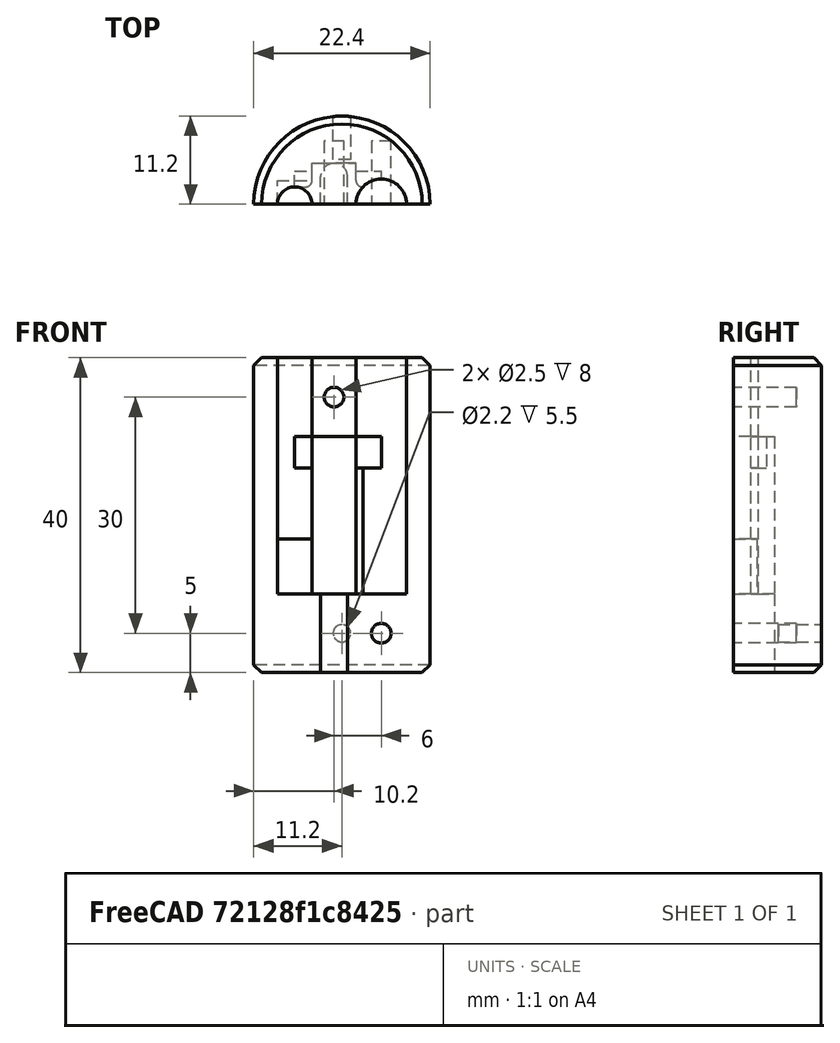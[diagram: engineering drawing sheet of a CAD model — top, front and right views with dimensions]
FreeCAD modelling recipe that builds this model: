
FCSTD DOCUMENT  (FreeCAD 0.21R33771 (Git))
Label: J-Pole_433_Bot2
Comment: J-Pole antenna bottom shell 2 (cable leading part)
License: CC BY-SA 4.0 (SPDX-ID: CC-BY-SA-4.0)
LicenseURL: https://creativecommons.org/licenses/by-sa/4.0/legalcode.txt
objects: Sketcher::SketchObject×9, PartDesign::Pocket×8, PartDesign::Fillet×2, PartDesign::Pad×1, PartDesign::Chamfer×1, PartDesign::Body×1, Mesh::Feature×1
note: 34 computed .brp shape members not serialized (recipe doc carries the construction recipe); baked Part::Feature solids carry a one-line shape summary decoded from their .brp

FEATURE [Sketcher::SketchObject] Sketch
  FullyConstrained = true
  MapMode = 5
  Support = -> [XY_Plane]
  sketch-geometry (2):
    g0: LineSegment StartX=-11.2 StartY=-2.98e-14 StartZ=0 EndX=11.2 EndY=-2.98e-14 EndZ=0
    g1: ArcOfCircle CenterX=0 CenterY=0 CenterZ=0 NormalX=0 NormalY=0 NormalZ=1 AngleXU=0 Radius=11.2 StartAngle=-2.7e-15 EndAngle=3.14159
  constraints (6):
    c: PointOnObject(g0,g-1)
    c: Horizontal(g0)
    c: Coincident(g1,g-1)
    c: Coincident(g1,g0)
    c: Coincident(g1,g0)
    c: Radius(g1) = 11.2
FEATURE [PartDesign::Pad] Pad
  Direction = (0,0,1)
  Length = 40
  Length2 = 10
  Profile = -> Sketch
  ReferenceAxis = -> Sketch [N_Axis]
  Type = 0
FEATURE [Sketcher::SketchObject] Sketch001
  ExternalGeometry = -> [Pad]
  FullyConstrained = true
  MapMode = 5
  Placement = pos=(0,0,40) rot=(0,0,1;0rad)
  Support = -> [Pad]
  sketch-geometry (2):
    g0: Circle CenterX=-6 CenterY=-2.98e-14 CenterZ=0 NormalX=0 NormalY=0 NormalZ=1 AngleXU=0 Radius=2.2
    g1: Circle CenterX=5 CenterY=-2.98e-14 CenterZ=0 NormalX=0 NormalY=0 NormalZ=1 AngleXU=0 Radius=3.2
  constraints (6):
    c: PointOnObject(g0,g-3)
    c: PointOnObject(g1,g-3)
    c: Radius(g1) = 3.2
    c: Radius(g0) = 2.2
    c: Distance(g-1,g0) = 6
    c: Distance(g-1,g1) = 5
FEATURE [PartDesign::Pocket] Pocket
  BaseFeature = -> Pad
  Direction = (0,0,-1)
  Length = 30
  Length2 = 5
  Profile = -> Sketch001
  ReferenceAxis = -> Sketch001 [N_Axis]
  Type = 0
FEATURE [Sketcher::SketchObject] Sketch002
  ExternalGeometry = -> [Pocket]
  FullyConstrained = true
  MapMode = 5
  Placement = pos=(0,-2.98e-14,0) rot=(1,0,0;1.5708rad)
  Support = -> [Pocket]
  sketch-geometry (4):
    g0: LineSegment StartX=-6 StartY=30 StartZ=0 EndX=5 EndY=30 EndZ=0
    g1: LineSegment StartX=5 StartY=30 StartZ=0 EndX=5 EndY=10 EndZ=0
    g2: LineSegment StartX=5 StartY=10 StartZ=0 EndX=-6 EndY=10 EndZ=0
    g3: LineSegment StartX=-6 StartY=10 StartZ=0 EndX=-6 EndY=30 EndZ=0
  constraints (12):
    c: Coincident(g0,g1)
    c: Coincident(g1,g2)
    c: Coincident(g2,g3)
    c: Coincident(g3,g0)
    c: Horizontal(g0)
    c: Horizontal(g2)
    c: Vertical(g1)
    c: Vertical(g3)
    c: PointOnObject(g-3,g2)
    c: DistanceX(g-2,g2) = -6
    c: DistanceX(g-2,g1) = 5
    c: DistanceY(g1,g1) = 20
FEATURE [PartDesign::Pocket] Pocket001
  BaseFeature = -> Pocket
  Direction = (0,1,-2e-16)
  Length = 2.2
  Length2 = 5
  Profile = -> Sketch002
  ReferenceAxis = -> Sketch002 [N_Axis]
  Type = 0
FEATURE [Sketcher::SketchObject] Sketch003
  ExternalGeometry = -> [Pocket001]
  FullyConstrained = true
  MapMode = 5
  Placement = pos=(0,-2.98e-14,0) rot=(1,0,0;1.5708rad)
  Support = -> [Pocket001]
  sketch-geometry (4):
    g0: LineSegment StartX=-2.7 StartY=10 StartZ=0 EndX=0.7 EndY=10 EndZ=0
    g1: LineSegment StartX=0.7 StartY=10 StartZ=0 EndX=0.7 EndY=0 EndZ=0
    g2: LineSegment StartX=0.7 StartY=0 StartZ=0 EndX=-2.7 EndY=0 EndZ=0
    g3: LineSegment StartX=-2.7 StartY=0 StartZ=0 EndX=-2.7 EndY=10 EndZ=0
  constraints (12):
    c: Coincident(g0,g1)
    c: Coincident(g1,g2)
    c: Coincident(g2,g3)
    c: Coincident(g3,g0)
    c: Horizontal(g0)
    c: Horizontal(g2)
    c: Vertical(g1)
    c: Vertical(g3)
    c: PointOnObject(g0,g-3)
    c: PointOnObject(g1,g-1)
    c: DistanceX(g2,g2) = 3.4
    c: Distance(g0,g-3) = 1.1
FEATURE [PartDesign::Pocket] Pocket002
  BaseFeature = -> Pocket001
  Direction = (0,1,-2e-16)
  Length = 2.2
  Length2 = 5
  Profile = -> Sketch003
  ReferenceAxis = -> Sketch003 [N_Axis]
  Type = 0
FEATURE [Sketcher::SketchObject] Sketch004
  ExternalGeometry = -> [Pocket002]
  FullyConstrained = true
  MapMode = 5
  Placement = pos=(0,2.2,-5e-16) rot=(1,0,0;1.5708rad)
  Support = -> [Pocket002]
  sketch-geometry (8):
    g0: LineSegment StartX=-3.8 StartY=30 StartZ=0 EndX=-3.8 EndY=10 EndZ=0
    g1: LineSegment StartX=-3.8 StartY=10 StartZ=0 EndX=-2.7 EndY=10 EndZ=0
    g2: LineSegment StartX=-3.8 StartY=30 StartZ=0 EndX=1.8 EndY=30 EndZ=0
    g3: LineSegment StartX=1.8 StartY=30 StartZ=0 EndX=1.8 EndY=10 EndZ=0
    g4: LineSegment StartX=1.8 StartY=10 StartZ=0 EndX=0.7 EndY=10 EndZ=0
    g5: LineSegment StartX=0.7 StartY=10 StartZ=0 EndX=0.7 EndY=0 EndZ=0
    g6: LineSegment StartX=0.7 StartY=0 StartZ=0 EndX=-2.7 EndY=0 EndZ=0
    g7: LineSegment StartX=-2.7 StartY=0 StartZ=0 EndX=-2.7 EndY=10 EndZ=0
  constraints (19):
    c: Coincident(g0,g-6)
    c: PointOnObject(g0,g-7)
    c: Vertical(g0)
    c: Coincident(g1,g0)
    c: Coincident(g1,g-7)
    c: Coincident(g2,g0)
    c: Coincident(g2,g-6)
    c: Coincident(g3,g2)
    c: PointOnObject(g3,g-8)
    c: Vertical(g3)
    c: PointOnObject(g4,g3)
    c: Coincident(g4,g-8)
    c: Horizontal(g4)
    c: Coincident(g5,g4)
    c: Coincident(g5,g-5)
    c: Coincident(g6,g5)
    c: Coincident(g6,g-4)
    c: Coincident(g7,g6)
    c: Coincident(g7,g1)
FEATURE [PartDesign::Pocket] Pocket003
  BaseFeature = -> Pocket002
  Direction = (0,1,-2e-16)
  Length = 3
  Length2 = 5
  Profile = -> Sketch004
  ReferenceAxis = -> Sketch004 [N_Axis]
  Type = 0
FEATURE [PartDesign::Fillet] Fillet
  Base = -> Pocket003 [Edge66,Edge49]
  BaseFeature = -> Pocket003
  Radius = 0.8
  SupportTransform = false
  UseAllEdges = false
FEATURE [PartDesign::Fillet] Fillet001
  Base = -> Fillet [Edge40,Edge38]
  BaseFeature = -> Fillet
  Radius = 1.699
  SupportTransform = false
  UseAllEdges = false
FEATURE [Sketcher::SketchObject] Sketch005
  ExternalGeometry = -> [Fillet001]
  FullyConstrained = true
  MapMode = 5
  Placement = pos=(0,-2.98e-14,0) rot=(1,0,0;1.5708rad)
  Support = -> [Fillet001]
  sketch-geometry (2):
    g0: Circle CenterX=-1 CenterY=35 CenterZ=0 NormalX=0 NormalY=0 NormalZ=1 AngleXU=0 Radius=1.25
    g1: Circle CenterX=5 CenterY=5 CenterZ=0 NormalX=0 NormalY=0 NormalZ=1 AngleXU=0 Radius=1.25
  constraints (6):
    c: Equal(g0,g1)
    c: Radius(g0) = 1.25
    c: DistanceX(g-2,g0) = -1
    c: DistanceX(g-2,g1) = 5
    c: DistanceY(g-1,g1) = 5
    c: Distance(g0,g-3) = 5
FEATURE [PartDesign::Pocket] Pocket004
  BaseFeature = -> Fillet001
  Direction = (0,1,-2e-16)
  Length = 8
  Length2 = 5
  Profile = -> Sketch005
  ReferenceAxis = -> Sketch005 [N_Axis]
  Type = 0
FEATURE [Sketcher::SketchObject] Sketch006
  AttachmentOffset = pos=(0,0,-11.2) rot=(0,0,1;0rad)
  FullyConstrained = true
  MapMode = 5
  Placement = pos=(0,11.2,2.5e-15) rot=(1,0,0;1.5708rad)
  Support = -> [XZ_Plane]
  sketch-geometry (1):
    g0: Circle CenterX=0 CenterY=5 CenterZ=0 NormalX=0 NormalY=0 NormalZ=1 AngleXU=0 Radius=1.1
  constraints (3):
    c: PointOnObject(g0,g-2)
    c: Radius(g0) = 1.1
    c: DistanceY(g-1,g0) = 5
FEATURE [PartDesign::Pocket] Pocket005
  BaseFeature = -> Pocket004
  Direction = (0,1,-2e-16)
  Length = 5.5
  Length2 = 5
  Profile = -> Sketch006
  ReferenceAxis = -> Sketch006 [N_Axis]
  Reversed = true
  Type = 0
FEATURE [Sketcher::SketchObject] Sketch007
  ExternalGeometry = -> [Pocket005]
  FullyConstrained = true
  MapMode = 5
  Placement = pos=(0,-2.98e-14,0) rot=(1,0,0;1.5708rad)
  Support = -> [Pocket005]
  sketch-geometry (4):
    g0: LineSegment StartX=-8.2 StartY=10 StartZ=0 EndX=-3.2 EndY=10 EndZ=0
    g1: LineSegment StartX=-3.2 StartY=10 StartZ=0 EndX=-3.2 EndY=17 EndZ=0
    g2: LineSegment StartX=-3.2 StartY=17 StartZ=0 EndX=-8.2 EndY=17 EndZ=0
    g3: LineSegment StartX=-8.2 StartY=17 StartZ=0 EndX=-8.2 EndY=10 EndZ=0
  constraints (11):
    c: Coincident(g0,g1)
    c: Coincident(g1,g2)
    c: Coincident(g2,g3)
    c: Coincident(g3,g0)
    c: Horizontal(g0)
    c: Horizontal(g2)
    c: Vertical(g1)
    c: Vertical(g3)
    c: Coincident(g0,g-3)
    c: DistanceY(g1,g1) = 7
    c: DistanceX(g2,g2) = 5
FEATURE [PartDesign::Pocket] Pocket006
  BaseFeature = -> Pocket005
  Direction = (0,1,-2e-16)
  Length = 3
  Length2 = 5
  Profile = -> Sketch007
  ReferenceAxis = -> Sketch007 [N_Axis]
  Type = 0
FEATURE [PartDesign::Chamfer] Chamfer
  Angle = 45
  Base = -> Pocket006 [Edge78,Edge34]
  BaseFeature = -> Pocket006
  ChamferType = 0
  FlipDirection = false
  Size = 1
  Size2 = 1
  SupportTransform = false
  UseAllEdges = false
FEATURE [Sketcher::SketchObject] Sketch008
  ExternalGeometry = -> [Chamfer]
  FullyConstrained = true
  MapMode = 5
  Placement = pos=(0,2.2,-5e-16) rot=(1,0,0;1.5708rad)
  Support = -> [Chamfer]
  sketch-geometry (4):
    g0: LineSegment StartX=-6 StartY=30 StartZ=0 EndX=5 EndY=30 EndZ=0
    g1: LineSegment StartX=5 StartY=30 StartZ=0 EndX=5 EndY=26 EndZ=0
    g2: LineSegment StartX=5 StartY=26 StartZ=0 EndX=-6 EndY=26 EndZ=0
    g3: LineSegment StartX=-6 StartY=26 StartZ=0 EndX=-6 EndY=30 EndZ=0
  constraints (11):
    c: Coincident(g0,g1)
    c: Coincident(g1,g2)
    c: Coincident(g2,g3)
    c: Coincident(g3,g0)
    c: Horizontal(g0)
    c: Horizontal(g2)
    c: Vertical(g1)
    c: Vertical(g3)
    c: Coincident(g0,g-3)
    c: DistanceX(g2,g2) = 11
    c: DistanceY(g3,g3) = 4
FEATURE [PartDesign::Pocket] Pocket007
  BaseFeature = -> Chamfer
  Direction = (0,1,-2e-16)
  Length = 2
  Length2 = 5
  Profile = -> Sketch008
  ReferenceAxis = -> Sketch008 [N_Axis]
  Type = 0
FEATURE [PartDesign::Body] Body
  Group = -> [Sketch,Pad,Sketch001,Pocket,Sketch002,Pocket001,Sketch003,Pocket002,Sketch004,Pocket003,Fillet,Fillet001,Sketch005,Pocket004,Sketch006,Pocket005,Sketch007,Pocket006,Chamfer,Sketch008,Pocket007]
  Origin = -> Origin
  Tip = -> Pocket007
FEATURE [Mesh::Feature] Mesh  label="J-Pole_433_Bot2"
